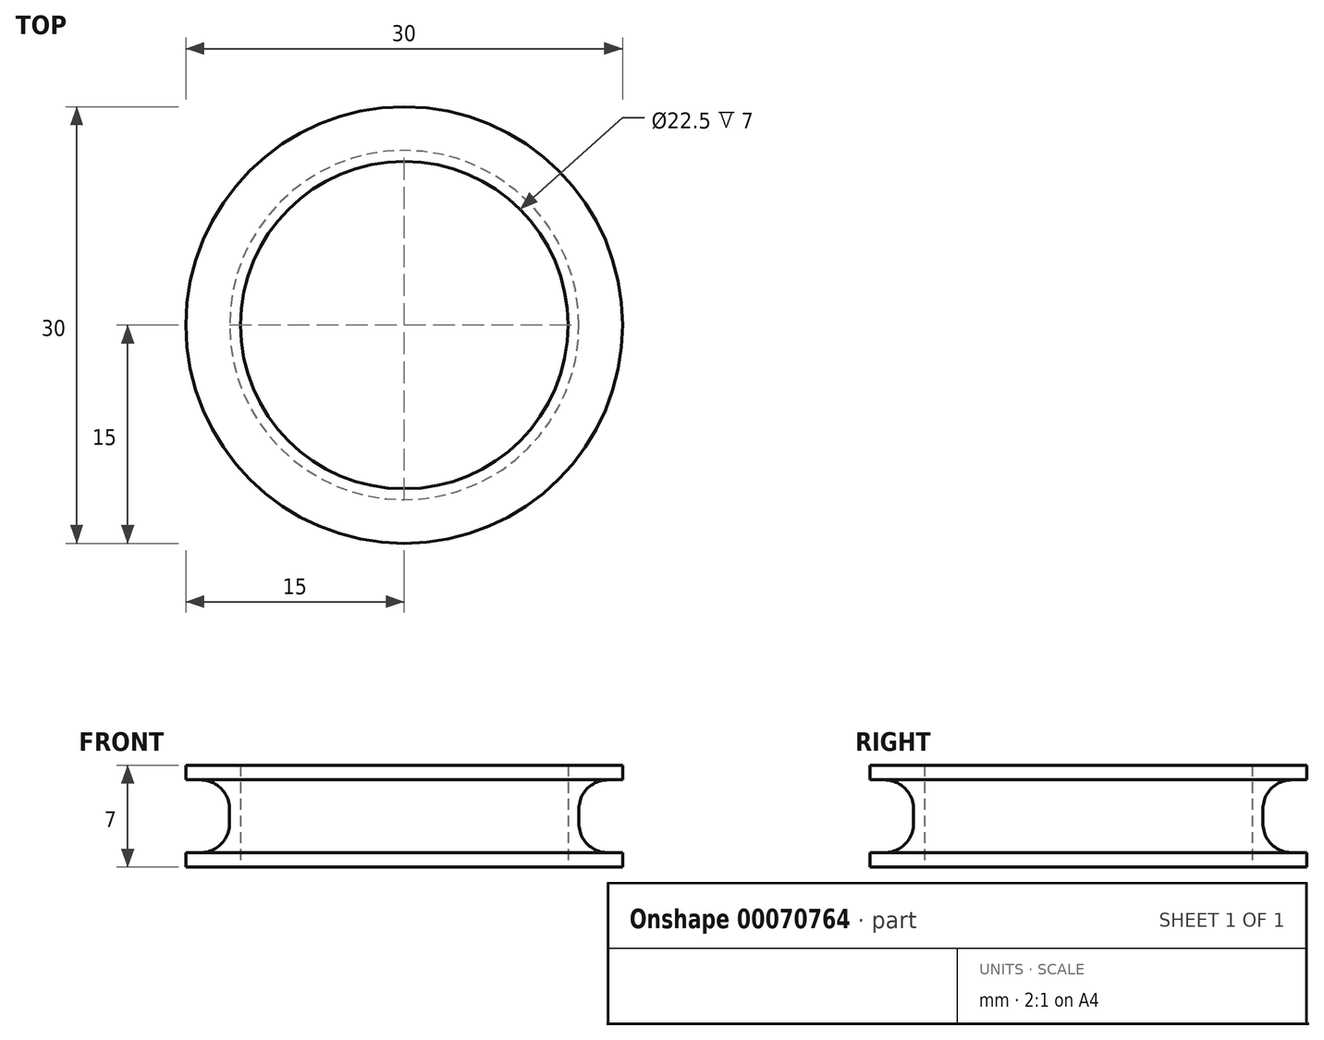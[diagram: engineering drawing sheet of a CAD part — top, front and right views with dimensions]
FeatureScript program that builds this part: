
annotation { "Feature Type Name" : "Feature", "Feature Type Description" : "" }
export const myFeature = defineFeature(function(context is Context, id is Id, definition is map)
    precondition{}
    {
        {
            var Q0;
            Q0=qCreatedBy(makeId("Top.planeOp"),FACE);
            var sketch = newSketch(context, id + "F0", { "sketchPlane" : qUnion([Q0])});
            skCircle(sketch, "E0", {"center": v(0, 0) * mm, "radius": 12 * mm});
            skCircle(sketch, "E1", {"center": v(0, 0) * mm, "radius": 11.25 * mm});
            skCircle(sketch, "E2", {"center": v(0, 0) * mm, "radius": 15 * mm});
            skSolve(sketch);
        }
        {
            var Q0;
            Q0=makeQuery(id+"F0.imprint","IMPRINT",FACE,{"disambiguationData":[TD([[makeQuery(id+"F0.imprint","IMPRINT",EDGE,{"derivedFrom":sQuery(id+"F0.wireOp",EDGE,"E0")}),-1.0]])]});
            extrude(context, id + "F1", {"entities" : qUnion([Q0]), "depth" : 1 * mm});
        }
        {
            var Q0;
            Q0=makeQuery(id+"F0.imprint","IMPRINT",FACE,{"disambiguationData":[TD([[makeQuery(id+"F0.imprint","IMPRINT",EDGE,{"derivedFrom":sQuery(id+"F0.wireOp",EDGE,"E0")}),1.0]])]});
            extrude(context, id + "F2", {"entities" : qUnion([Q0]), "operationType" : NewBodyOperationType.ADD, "depth" : 7 * mm});
        }
        {
            var Q0;
            Q0=makeQuery(id+"F1.opExtrude","CAP_FACE",FACE,{"disambiguationData":[OSD([sQuery(id+"F0.wireOp",EDGE,"E1"),sQuery(id+"F0.wireOp",EDGE,"E2")])],"isStart":false});
            extrude(context, id + "F3", {"entities" : qUnion([Q0]), "operationType" : NewBodyOperationType.ADD, "depth" : 6 * mm, "hasSecondDirection" : true, "secondDirectionOppositeDirection" : false, "secondDirectionDepth" : 5 * mm});
        }
        {
            var Q0;
            Q0=makeQuery(id+"F2.opExtrude","SWEPT_FACE",FACE,{"disambiguationData":[OSD([sQuery(id+"F0.wireOp",EDGE,"E0")])]});
            fillet(context, id + "F4", {"entities" : qUnion([Q0]), "radius" : 2 * mm, "tangentPropagation" : true, "allowEdgeOverflow" : false});
        }
    });
